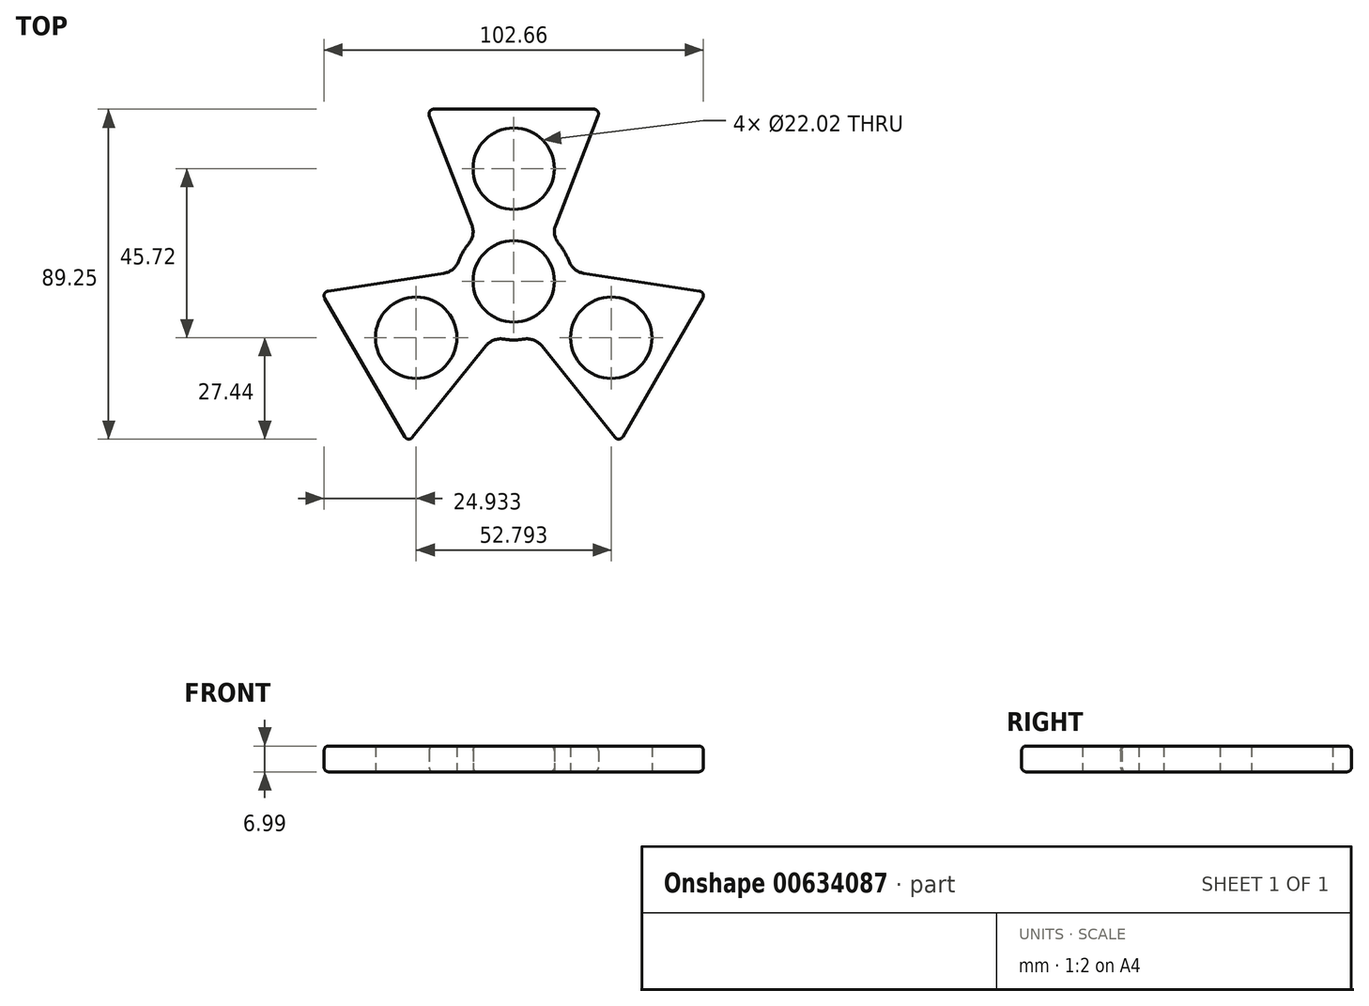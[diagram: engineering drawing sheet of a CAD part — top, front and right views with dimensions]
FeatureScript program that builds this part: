
annotation { "Feature Type Name" : "Feature", "Feature Type Description" : "" }
export const myFeature = defineFeature(function(context is Context, id is Id, definition is map)
    precondition{}
    {
        {
            var Q0;
            Q0=qCreatedBy(makeId("Top.planeOp"),FACE);
            var sketch = newSketch(context, id + "F0", { "sketchPlane" : qUnion([Q0])});
            skCircle(sketch, "E0", {"center": v(0, 0) * mm, "radius": 11.01 * mm});
            skLineSegment(sketch, "E1", {"start": v(0, 0) * mm, "end": v(0, 30.48) * mm});
            skCircle(sketch, "E2", {"center": v(0, 30.48) * mm, "radius": 11.01 * mm});
            skCircle(sketch, "E3", {"center": v(0, 0) * mm, "radius": 15.88 * mm});
            skLineSegment(sketch, "E4", {"start": v(-10.16, 12.2) * mm, "end": v(-23.51, 46.57) * mm});
            skLineSegment(sketch, "E5", {"start": v(-23.51, 46.57) * mm, "end": v(23.51, 46.57) * mm});
            skLineSegment(sketch, "E6", {"start": v(23.51, 46.57) * mm, "end": v(10.16, 12.2) * mm});
            skLineSegment(sketch, "E7.1.0", {"start": v(-5.48, -14.9) * mm, "end": v(-28.57, -43.65) * mm});
            skLineSegment(sketch, "E7.1.1", {"start": v(-28.57, -43.65) * mm, "end": v(-52.09, -2.92) * mm});
            skCircle(sketch, "E7.1.2", {"center": v(-26.4, -15.24) * mm, "radius": 11.01 * mm});
            skLineSegment(sketch, "E7.1.3", {"start": v(-52.09, -2.92) * mm, "end": v(-15.64, 2.7) * mm});
            skLineSegment(sketch, "E7.1.4", {"start": v(0, 0) * mm, "end": v(-26.4, -15.24) * mm});
            skLineSegment(sketch, "E7.2.0", {"start": v(15.64, 2.7) * mm, "end": v(52.09, -2.92) * mm});
            skLineSegment(sketch, "E7.2.1", {"start": v(52.09, -2.92) * mm, "end": v(28.57, -43.65) * mm});
            skCircle(sketch, "E7.2.2", {"center": v(26.4, -15.24) * mm, "radius": 11.01 * mm});
            skLineSegment(sketch, "E7.2.3", {"start": v(28.57, -43.65) * mm, "end": v(5.48, -14.9) * mm});
            skLineSegment(sketch, "E7.2.4", {"start": v(0, 0) * mm, "end": v(26.4, -15.24) * mm});
            skPoint(sketch, "E8", {"position": v(0, 46.57) * mm});
            skLineSegment(sketch, "E9", {"start": v(0, 30.48) * mm, "end": v(0, 46.57) * mm});
            skLineSegment(sketch, "E10", {"start": v(0, 0) * mm, "end": v(0, -15.88) * mm});
            skSolve(sketch);
        }
        {
            var Q0;
            Q0 = qSketchRegion(id + "F0", true);
            extrude(context, id + "F1", {"entities" : qUnion([Q0]), "depth" : 7 * mm, "offsetDistance" : 25.4 * mm});
        }
        {
            var Q0;
            Q0=makeQuery(id+"F1.opExtrude","SWEPT_EDGE",EDGE,{"disambiguationData":[OSD([sQuery(id+"F0.wireOp",EDGE,"E3"),sQuery(id+"F0.wireOp",EDGE,"E7.2.0")])]});
            var Q1;
            Q1=makeQuery(id+"F1.opExtrude","SWEPT_EDGE",EDGE,{"disambiguationData":[OSD([sQuery(id+"F0.wireOp",EDGE,"E3"),sQuery(id+"F0.wireOp",EDGE,"E6")])]});
            var Q2;
            Q2=makeQuery(id+"F1.opExtrude","SWEPT_EDGE",EDGE,{"disambiguationData":[OSD([sQuery(id+"F0.wireOp",EDGE,"E3"),sQuery(id+"F0.wireOp",EDGE,"E7.2.3")])]});
            var Q3;
            Q3=makeQuery(id+"F1.opExtrude","SWEPT_EDGE",EDGE,{"disambiguationData":[OSD([sQuery(id+"F0.wireOp",EDGE,"E3"),sQuery(id+"F0.wireOp",EDGE,"E7.1.0")])]});
            var Q4;
            Q4=makeQuery(id+"F1.opExtrude","SWEPT_EDGE",EDGE,{"disambiguationData":[OSD([sQuery(id+"F0.wireOp",EDGE,"E3"),sQuery(id+"F0.wireOp",EDGE,"E7.1.3")])]});
            var Q5;
            Q5=makeQuery(id+"F1.opExtrude","SWEPT_EDGE",EDGE,{"disambiguationData":[OSD([sQuery(id+"F0.wireOp",EDGE,"E3"),sQuery(id+"F0.wireOp",EDGE,"E4")])]});
            fillet(context, id + "F2", {"entities" : qUnion([Q0, Q1, Q2, Q3, Q4, Q5]), "radius" : 5.08 * mm, "tangentPropagation" : true, "allowEdgeOverflow" : false});
        }
        {
            var Q0;
            Q0=makeQuery(id+"F1.opExtrude","SWEPT_EDGE",EDGE,{"disambiguationData":[OSD([sQuery(id+"F0.wireOp",EDGE,"E7.2.0"),sQuery(id+"F0.wireOp",EDGE,"E7.2.1")])]});
            var Q1;
            Q1=makeQuery(id+"F1.opExtrude","SWEPT_EDGE",EDGE,{"disambiguationData":[OSD([sQuery(id+"F0.wireOp",EDGE,"E7.2.1"),sQuery(id+"F0.wireOp",EDGE,"E7.2.3")])]});
            var Q2;
            Q2=makeQuery(id+"F1.opExtrude","SWEPT_EDGE",EDGE,{"disambiguationData":[OSD([sQuery(id+"F0.wireOp",EDGE,"E7.1.0"),sQuery(id+"F0.wireOp",EDGE,"E7.1.1")])]});
            var Q3;
            Q3=makeQuery(id+"F1.opExtrude","SWEPT_EDGE",EDGE,{"disambiguationData":[OSD([sQuery(id+"F0.wireOp",EDGE,"E5"),sQuery(id+"F0.wireOp",EDGE,"E6")])]});
            var Q4;
            Q4=makeQuery(id+"F1.opExtrude","SWEPT_EDGE",EDGE,{"disambiguationData":[OSD([sQuery(id+"F0.wireOp",EDGE,"E4"),sQuery(id+"F0.wireOp",EDGE,"E5")])]});
            var Q5;
            Q5=makeQuery(id+"F1.opExtrude","SWEPT_EDGE",EDGE,{"disambiguationData":[OSD([sQuery(id+"F0.wireOp",EDGE,"E7.1.1"),sQuery(id+"F0.wireOp",EDGE,"E7.1.3")])]});
            fillet(context, id + "F3", {"entities" : qUnion([Q0, Q1, Q2, Q3, Q4, Q5]), "radius" : 1.27 * mm, "tangentPropagation" : true, "allowEdgeOverflow" : false});
        }
        {
            var Q0;
            Q0=makeQuery(id+"F1.opExtrude","CAP_EDGE",EDGE,{"disambiguationData":[OSD([sQuery(id+"F0.wireOp",EDGE,"E7.2.1")])],"isStart":false});
            fillet(context, id + "F4", {"entities" : qUnion([Q0]), "radius" : 1.27 * mm, "tangentPropagation" : true, "allowEdgeOverflow" : false});
        }
        {
            var Q0;
            Q0=makeQuery(id+"F1.opExtrude","CAP_EDGE",EDGE,{"disambiguationData":[OSD([sQuery(id+"F0.wireOp",EDGE,"E7.1.3")])],"isStart":true});
            fillet(context, id + "F5", {"entities" : qUnion([Q0]), "radius" : 1.27 * mm, "tangentPropagation" : true, "allowEdgeOverflow" : false});
        }
    });
